FCSTD DOCUMENT  (FreeCAD 1.2R20251216 (Git shallow))
Label: MainAssembly
License: All rights reserved
objects: App::Link×10, App::FeaturePython×8, App::Point×3, Assembly::AssemblyLink×2, Assembly::JointGroup×1, Assembly::AssemblyObject×1
EXTERNAL_REF file=BaseAssembly.FCStd obj=Assembly
EXTERNAL_REF file=BaseAssembly.FCStd obj=Base
EXTERNAL_REF file=BaseAssembly.FCStd obj=Bracket
EXTERNAL_REF file=BaseAssembly.FCStd obj=Bracket001
EXTERNAL_REF file=assembly/BasePart.FCStd obj=Body002

FEATURE [App::Point] Origin001
  Role = Origin
FEATURE [App::Point] Origin003
  Role = Origin
FEATURE [App::Link] Base
  LinkPlacement = pos=(-8,9.53674e-07,0) rot=(0,0,1;0rad)
  LinkedObject = -> <external BaseAssembly.FCStd>#Base
  Placement = pos=(-8,9.53674e-07,0) rot=(0,0,1;0rad)
FEATURE [App::Link] Bracket
  LinkPlacement = pos=(-33,9.53674e-07,5) rot=(0,0,1;0rad)
  LinkedObject = -> <external BaseAssembly.FCStd>#Bracket
  Placement = pos=(-33,9.53674e-07,5) rot=(0,0,1;0rad)
FEATURE [App::Link] Bracket001
  LinkPlacement = pos=(17,9.53674e-07,5) rot=(0,0,1;3.14159rad)
  LinkedObject = -> <external BaseAssembly.FCStd>#Bracket001
  Placement = pos=(17,9.53674e-07,5) rot=(0,0,1;3.14159rad)
FEATURE [Assembly::AssemblyLink] Assembly001  label="Assembly"
  Group = -> [Base,Bracket,Bracket001]
  LinkedObject = -> <external BaseAssembly.FCStd>#Assembly
  Origin = -> Origin002
  Placement = pos=(0,17.655,0) rot=(0,-1,0;0.007806rad)
  Rigid = true
FEATURE [App::FeaturePython] GroundedJoint  # Assembly grounded joint (typed FeaturePython)
  ObjectToGround = -> Assembly001
FEATURE [App::Point] Origin005  label="Origin006"
  Role = Origin
FEATURE [App::Link] Base001
  LinkPlacement = pos=(-8,9.53674e-07,0) rot=(0,0,1;0rad)
  LinkedObject = -> <external BaseAssembly.FCStd>#Base
  Placement = pos=(-8,9.53674e-07,0) rot=(0,0,1;0rad)
FEATURE [App::Link] Bracket002
  LinkPlacement = pos=(-33,9.53674e-07,5) rot=(0,0,1;0rad)
  LinkedObject = -> <external BaseAssembly.FCStd>#Bracket
  Placement = pos=(-33,9.53674e-07,5) rot=(0,0,1;0rad)
FEATURE [App::Link] Bracket003
  LinkPlacement = pos=(17,9.53674e-07,5) rot=(0,0,1;3.14159rad)
  LinkedObject = -> <external BaseAssembly.FCStd>#Bracket001
  Placement = pos=(17,9.53674e-07,5) rot=(0,0,1;3.14159rad)
FEATURE [Assembly::AssemblyLink] Assembly002  label="Assembly 1"
  Group = -> [Base001,Bracket002,Bracket003]
  LinkedObject = -> <external BaseAssembly.FCStd>#Assembly
  Origin = -> Origin004
  Placement = pos=(-0.0157594,146.637,-0.000123025) rot=(0.003785,-0.244485,-0.969646;0.031927rad)
  Rigid = true
FEATURE [App::FeaturePython] Joint  label="Slider"  # Assembly joint (typed FeaturePython)
  Angle = 0
  AngleMax = 0
  AngleMin = 0
  Detach1 = false
  Detach2 = false
  Distance = 0
  Distance2 = 0
  EnableAngleMax = false
  EnableAngleMin = false
  EnableLengthMax = true
  EnableLengthMin = true
  JointType = 3 (Slider)
  LengthMax = 130
  LengthMin = 60
  Placement1 = pos=(-24.8905,0,5) rot=(0.57735,0.57735,0.57735;4.18879rad)
  Placement2 = pos=(-24.8905,0,5) rot=(0.57735,0.57735,0.57735;4.18879rad)
  Reference1 = -> Assembly [Assembly001.Base.Edge12,Assembly001.Base.Edge12]
  Reference2 = -> Assembly [Assembly002.Base001.Edge12,Assembly002.Base001.Edge12]
  Suppressed = false
FEATURE [App::Link] Link
  LinkPlacement = pos=(-31.3123,17.7165,39.7568) rot=(0.312496,0.888118,-0.337035;4.57501rad)
  LinkedObject = -> <external assembly/BasePart.FCStd>#Body002
  Placement = pos=(-31.3123,17.7165,39.7568) rot=(0.312496,0.888118,-0.337035;4.57501rad)
FEATURE [App::FeaturePython] Joint001  label="Revolute"  # Assembly joint (typed FeaturePython)
  Angle = 0
  AngleMax = 0
  AngleMin = 0
  Detach1 = false
  Detach2 = false
  Distance = 0
  Distance2 = 0
  EnableAngleMax = false
  EnableAngleMin = false
  EnableLengthMax = false
  EnableLengthMin = false
  JointType = 1 (Revolute)
  LengthMax = 0
  LengthMin = 0
  Placement1 = pos=(0,-5.3e-15,2) rot=(0,0,1;0rad)
  Placement2 = pos=(0,0,35) rot=(0.57735,0.57735,0.57735;2.0944rad)
  Reference1 = -> Assembly [Link.Edge15,Link.Edge15]
  Reference2 = -> Assembly [Assembly001.Bracket.Edge45,Assembly001.Bracket.Edge45]
  Suppressed = false
FEATURE [App::Link] Link001
  LinkPlacement = pos=(-31.9056,82.7182,115.773) rot=(-0.680956,-0.263231,0.68338;2.66999rad)
  LinkedObject = -> <external assembly/BasePart.FCStd>#Body002
  Placement = pos=(-31.9056,82.7182,115.773) rot=(-0.680956,-0.263231,0.68338;2.66999rad)
FEATURE [App::FeaturePython] Joint002  label="Revolute001"  # Assembly joint (typed FeaturePython)
  Angle = 0
  AngleMax = 0
  AngleMin = 0
  Detach1 = false
  Detach2 = false
  Distance = 0
  Distance2 = 0
  EnableAngleMax = false
  EnableAngleMin = false
  EnableLengthMax = false
  EnableLengthMin = false
  JointType = 1 (Revolute)
  LengthMax = 0
  LengthMin = 0
  Placement1 = pos=(100,2.84e-14,3.6e-15) rot=(0,0,1;0rad)
  Placement2 = pos=(0,0,35) rot=(0.57735,0.57735,0.57735;2.0944rad)
  Reference1 = -> Assembly [Link001.Edge17,Link001.Edge17]
  Reference2 = -> Assembly [Assembly002.Bracket002.Edge45,Assembly002.Bracket002.Edge45]
  Suppressed = false
FEATURE [App::FeaturePython] Joint003  label="Revolute002"  # Assembly joint (typed FeaturePython)
  Angle = 0
  AngleMax = 0
  AngleMin = 0
  Detach1 = false
  Detach2 = false
  Distance = 0
  Distance2 = 0
  EnableAngleMax = false
  EnableAngleMin = false
  EnableLengthMax = false
  EnableLengthMin = false
  JointType = 1 (Revolute)
  LengthMax = 0
  LengthMin = 0
  Placement1 = pos=(-1.42e-14,0,2) rot=(0,0,1;0rad)
  Placement2 = pos=(100,3.6e-15,-3.6e-15) rot=(0,0,1;0rad)
  Reference1 = -> Assembly [Link001.Edge15,Link001.Edge15]
  Reference2 = -> Assembly [Link.Edge17,Link.Edge17]
  Suppressed = false
FEATURE [App::Link] Link002
  LinkPlacement = pos=(16.0768,81.8829,116.802) rot=(-0.307622,0.88959,-0.337636;1.69094rad)
  LinkedObject = -> <external assembly/BasePart.FCStd>#Body002
  Placement = pos=(16.0768,81.8829,116.802) rot=(-0.307622,0.88959,-0.337636;1.69094rad)
FEATURE [App::FeaturePython] Joint004  label="Revolute003"  # Assembly joint (typed FeaturePython)
  Angle = 0
  AngleMax = 0
  AngleMin = 0
  Detach1 = false
  Detach2 = false
  Distance = 0
  Distance2 = 0
  EnableAngleMax = false
  EnableAngleMin = false
  EnableLengthMax = false
  EnableLengthMin = false
  JointType = 1 (Revolute)
  LengthMax = 0
  LengthMin = 0
  Placement1 = pos=(100,1.24e-14,2) rot=(0,0,1;0rad)
  Placement2 = pos=(0,0,35) rot=(0.57735,0.57735,0.57735;2.0944rad)
  Reference1 = -> Assembly [Link002.Edge18,Link002.Edge18]
  Reference2 = -> Assembly [Assembly001.Bracket001.Edge45,Assembly001.Bracket001.Edge45]
  Suppressed = false
FEATURE [App::Link] Link003
  LinkPlacement = pos=(18.6623,146.049,40.1469) rot=(-0.308356,0.891015,0.333179;4.57834rad)
  LinkedObject = -> <external assembly/BasePart.FCStd>#Body002
  Placement = pos=(18.6623,146.049,40.1469) rot=(-0.308356,0.891015,0.333179;4.57834rad)
FEATURE [App::FeaturePython] Joint005  label="Revolute004"  # Assembly joint (typed FeaturePython)
  Angle = 0
  AngleMax = 0
  AngleMin = 0
  Detach1 = false
  Detach2 = false
  Distance = 0
  Distance2 = 0
  EnableAngleMax = false
  EnableAngleMin = false
  EnableLengthMax = false
  EnableLengthMin = false
  JointType = 1 (Revolute)
  LengthMax = 0
  LengthMin = 0
  Placement1 = pos=(0,0,2) rot=(0,0,1;0rad)
  Placement2 = pos=(0,0,35) rot=(0.57735,0.57735,0.57735;2.0944rad)
  Reference1 = -> Assembly [Link003.Edge15,Link003.Edge15]
  Reference2 = -> Assembly [Assembly002.Bracket003.Edge45,Assembly002.Bracket003.Edge45]
  Suppressed = false
FEATURE [App::FeaturePython] Joint006  label="Revolute005"  # Assembly joint (typed FeaturePython)
  Angle = 0
  AngleMax = 0
  AngleMin = 0
  Detach1 = false
  Detach2 = false
  Distance = 0
  Distance2 = 0
  EnableAngleMax = false
  EnableAngleMin = false
  EnableLengthMax = false
  EnableLengthMin = false
  JointType = 1 (Revolute)
  LengthMax = 0
  LengthMin = 0
  Placement1 = pos=(100,0,1.8e-15) rot=(0,0,1;0rad)
  Reference1 = -> Assembly [Link003.Edge17,Link003.Edge17]
  Reference2 = -> Assembly [Link002.Edge3,Link002.Edge3]
  Suppressed = false
FEATURE [Assembly::JointGroup] Joints
  Group = -> [GroundedJoint,Joint,Joint001,Joint002,Joint003,Joint004,Joint005,Joint006]
FEATURE [Assembly::AssemblyObject] Assembly
  Group = -> [Joints,Assembly001,GroundedJoint,Assembly002,Joint,Link,Joint001,Link001,Joint002,Joint003,Link002,Joint004,Link003,Joint005,Joint006]
  Origin = -> Origin
  Type = Assembly

RESOLVED EXTERNAL PARTS (link-assembly join: the EXTERNAL_REF files above that resolve inside this repo's crawl, each included once):
---- part BaseAssembly.FCStd = doc fcstd_8ca3d356e84e ----
FCSTD DOCUMENT  (FreeCAD 1.2R20251216 (Git shallow))
Label: BaseAssembly
License: All rights reserved
objects: App::Link×3, App::FeaturePython×3, App::Point×1, Assembly::JointGroup×1, Assembly::AssemblyObject×1
EXTERNAL_REF file=assembly/BasePart.FCStd obj=Body
EXTERNAL_REF file=assembly/BasePart.FCStd obj=Body001

FEATURE [App::Point] Origin001
  Role = Origin
FEATURE [App::Link] Base
  LinkPlacement = pos=(-8,9.53674e-07,0) rot=(0,0,1;0rad)
  LinkedObject = -> <external assembly/BasePart.FCStd>#Body
  Placement = pos=(-8,9.53674e-07,0) rot=(0,0,1;0rad)
FEATURE [App::FeaturePython] GroundedJoint  # Assembly grounded joint (typed FeaturePython)
  ObjectToGround = -> Base
FEATURE [App::Link] Bracket001
  LinkPlacement = pos=(17,9.53674e-07,5) rot=(0,0,1;3.14159rad)
  LinkedObject = -> <external assembly/BasePart.FCStd>#Body001
  Placement = pos=(17,9.53674e-07,5) rot=(0,0,1;3.14159rad)
FEATURE [App::FeaturePython] Joint001  label="Fixed003"  # Assembly joint (typed FeaturePython)
  Angle = 0
  AngleMax = 0
  AngleMin = 0
  Detach1 = false
  Detach2 = false
  Distance = 0
  Distance2 = 0
  EnableAngleMax = false
  EnableAngleMin = false
  EnableLengthMax = false
  EnableLengthMin = false
  JointType = 0 (Fixed)
  LengthMax = 0
  LengthMin = 0
  Placement1 = pos=(-15,15,0) rot=(0,0,1;0rad)
  Placement2 = pos=(40,-15,5) rot=(0,1,0;3.14159rad)
  Reference1 = -> Assembly [Bracket001.Edge53,Bracket001.Edge53]
  Reference2 = -> Assembly [Base.Edge40,Base.Edge40]
  Suppressed = false
FEATURE [App::FeaturePython] Joint  label="Fixed002"  # Assembly joint (typed FeaturePython)
  Angle = 0
  AngleMax = 0
  AngleMin = 0
  Detach1 = false
  Detach2 = false
  Distance = 0
  Distance2 = 0
  EnableAngleMax = false
  EnableAngleMin = false
  EnableLengthMax = false
  EnableLengthMin = false
  JointType = 0 (Fixed)
  LengthMax = 0
  LengthMin = 0
  Placement1 = pos=(-15,-15,0) rot=(0,0,1;0rad)
  Placement2 = pos=(-40,-15,5) rot=(0,0,1;0rad)
  Reference1 = -> Assembly [Bracket.Edge52,Bracket.Edge52]
  Reference2 = -> Assembly [Base.Edge14,Base.Edge14]
  Suppressed = false
FEATURE [Assembly::JointGroup] Joints
  Group = -> [GroundedJoint,Joint,Joint001]
FEATURE [App::Link] Bracket
  LinkPlacement = pos=(-33,9.53674e-07,5) rot=(0,0,1;0rad)
  LinkedObject = -> <external assembly/BasePart.FCStd>#Body001
  Placement = pos=(-33,9.53674e-07,5) rot=(0,0,1;0rad)
FEATURE [Assembly::AssemblyObject] Assembly
  Group = -> [Joints,Base,GroundedJoint,Bracket,Joint,Bracket001,Joint001]
  Origin = -> Origin
  Type = Assembly
---- part assembly/BasePart.FCStd = doc fcstd_4848bd1dab05 ----
FCSTD DOCUMENT  (FreeCAD 1.2R20251216 (Git shallow))
Label: BasePart
License: All rights reserved
LicenseURL: https://en.wikipedia.org/wiki/All_rights_reserved
objects: Sketcher::SketchObject×6, PartDesign::Pad×5, PartDesign::Body×3, App::Point×3, PartDesign::Pocket×1, PartDesign::Mirrored×1, PartDesign::Chamfer×1
note: 38 computed .brp shape members not serialized (recipe doc carries the construction recipe); baked Part::Feature solids carry a one-line shape summary decoded from their .brp

FEATURE [Sketcher::SketchObject] Sketch
  ArcFitTolerance = 1e-06
  AttachmentSupport = -> [XY_Plane]
  ExternalTypes = [0]
  FullyConstrained = true
  MakeInternals = false
  MapMode = 5
  sketch-geometry (10):
    g0: LineSegment StartX=-50 StartY=15 StartZ=0 EndX=-50 EndY=-15 EndZ=0
    g1: LineSegment StartX=-40 StartY=-25 StartZ=0 EndX=0 EndY=-25 EndZ=0
    g2: LineSegment StartX=0 StartY=-25 StartZ=0 EndX=0 EndY=25 EndZ=0
    g3: LineSegment StartX=0 StartY=25 StartZ=0 EndX=-40 EndY=25 EndZ=0
    g4: ArcOfCircle CenterX=-40 CenterY=15 CenterZ=0 NormalX=0 NormalY=0 NormalZ=1 AngleXU=0 Radius=10 StartAngle=1.5708 EndAngle=3.14159
    g5: GeomPoint [constr] X=-50 Y=25 Z=0
    g6: ArcOfCircle CenterX=-40 CenterY=-15 CenterZ=0 NormalX=0 NormalY=0 NormalZ=1 AngleXU=0 Radius=10 StartAngle=3.14159 EndAngle=4.71239
    g7: GeomPoint [constr] X=-50 Y=-25 Z=0
    g8: Circle CenterX=-40 CenterY=15 CenterZ=0 NormalX=0 NormalY=0 NormalZ=1 AngleXU=0 Radius=5
    g9: Circle CenterX=-40 CenterY=-15 CenterZ=0 NormalX=0 NormalY=0 NormalZ=1 AngleXU=0 Radius=5
  constraints (23):
    c: Coincident(g1,g2)
    c: Coincident(g2,g3)
    c: Vertical(g0)
    c: Vertical(g2)
    c: Horizontal(g1)
    c: Horizontal(g3)
    c: Distance(g5,g2) = 50
    c: Distance(g7,g5) = 50
    c: Symmetric(g2,g1,g-1)
    c: PointOnObject(g5,g0)
    c: PointOnObject(g5,g3)
    c: Tangent(g0,g4) = -1.5708
    c: Tangent(g3,g4) = -1.5708
    c: PointOnObject(g7,g0)
    c: PointOnObject(g7,g1)
    c: Tangent(g0,g6) = -1.5708
    c: Tangent(g1,g6) = -1.5708
    c: Radius(g4) = 10
    c: Equal(g6,g4)
    c: Coincident(g8,g4)
    c: Coincident(g9,g6)
    c: Equal(g8,g9)
    c: Diameter(g8) = 10
FEATURE [PartDesign::Pad] Pad
  Direction = (0,0,1)
  Length = 5
  Length2 = 10
  Profile = -> Sketch
  ReferenceAxis = -> Sketch [N_Axis]
  Refine = true
  SideType = 0
  Suppressed = false
  Type = 0
  Type2 = 0
FEATURE [Sketcher::SketchObject] Sketch001
  ArcFitTolerance = 1e-06
  AttachmentSupport = -> [Pad]
  ExternalGeometry = -> [Pad]
  ExternalTypes = [0]
  FullyConstrained = true
  MakeInternals = false
  MapMode = 5
  Placement = pos=(0,-25,0) rot=(1,0,0;1.5708rad)
  sketch-geometry (4):
    g0: LineSegment StartX=0 StartY=3 StartZ=0 EndX=-24 EndY=3 EndZ=0
    g1: LineSegment StartX=-24 StartY=3 StartZ=0 EndX=-24.8905 EndY=5 EndZ=0
    g2: LineSegment StartX=-24.8905 StartY=5 StartZ=0 EndX=0 EndY=5 EndZ=0
    g3: LineSegment StartX=0 StartY=5 StartZ=0 EndX=0 EndY=3 EndZ=0
  constraints (11):
    c: PointOnObject(g0,g-2)
    c: Horizontal(g0)
    c: Coincident(g0,g1)
    c: PointOnObject(g1,g-3)
    c: Coincident(g1,g2)
    c: Coincident(g2,g-3)
    c: Coincident(g2,g3)
    c: Coincident(g3,g0)
    c: Distance(g3,g3) = 2
    c: DistanceX(g0,g0) = 24
    c: Angle(g0,g1) = 1.98968
FEATURE [PartDesign::Pocket] Pocket
  BaseFeature = -> Pad
  Direction = (0,1,-2e-16)
  Length = 5
  Length2 = 5
  Profile = -> Sketch001
  ReferenceAxis = -> Sketch001 [N_Axis]
  Refine = true
  SideType = 0
  Suppressed = false
  Type = 1
  Type2 = 0
FEATURE [PartDesign::Mirrored] Mirrored
  BaseFeature = -> Pocket
  MirrorPlane = -> YZ_Plane
  Refine = true
  Suppressed = false
  TransformMode = 1
FEATURE [PartDesign::Body] Body  label="Base"
  AllowCompound = false
  Group = -> [Sketch,Pad,Sketch001,Pocket,Mirrored]
  Origin = -> Origin
  Tip = -> Mirrored
FEATURE [Sketcher::SketchObject] Sketch002
  ArcFitTolerance = 1e-06
  AttachmentSupport = -> [XY_Plane001]
  ExternalTypes = [0]
  FullyConstrained = true
  MakeInternals = false
  MapMode = 5
  sketch-geometry (8):
    g0: LineSegment StartX=0 StartY=25 StartZ=0 EndX=-15 EndY=25 EndZ=0
    g1: ArcOfCircle CenterX=-15 CenterY=15 CenterZ=0 NormalX=0 NormalY=0 NormalZ=1 AngleXU=0 Radius=10 StartAngle=1.5708 EndAngle=3.14159
    g2: LineSegment StartX=-25 StartY=15 StartZ=0 EndX=-25 EndY=-15 EndZ=0
    g3: ArcOfCircle CenterX=-15 CenterY=-15 CenterZ=0 NormalX=0 NormalY=0 NormalZ=1 AngleXU=0 Radius=10 StartAngle=3.14159 EndAngle=4.71239
    g4: LineSegment StartX=-15 StartY=-25 StartZ=0 EndX=0 EndY=-25 EndZ=0
    g5: LineSegment StartX=0 StartY=-25 StartZ=0 EndX=0 EndY=25 EndZ=0
    g6: Circle CenterX=-15 CenterY=15 CenterZ=0 NormalX=0 NormalY=0 NormalZ=1 AngleXU=0 Radius=5
    g7: Circle CenterX=-15 CenterY=-15 CenterZ=0 NormalX=0 NormalY=0 NormalZ=1 AngleXU=0 Radius=5
  constraints (19):
    c: PointOnObject(g0,g-2)
    c: Tangent(g0,g1) = -1.5708
    c: Vertical(g2)
    c: Tangent(g2,g3) = -1.5708
    c: Tangent(g3,g4) = -1.5708
    c: Coincident(g4,g5)
    c: Coincident(g5,g0)
    c: Horizontal(g0)
    c: Horizontal(g4)
    c: Tangent(g1,g2) = -1.5708
    c: Coincident(g6,g1)
    c: Coincident(g7,g3)
    c: DistanceX(g1,g0) = 25
    c: DistanceY(g4,g0) = 50
    c: Diameter(g6) = 10
    c: Radius(g1) = 10
    c: Equal(g6,g7)
    c: Equal(g1,g3)
    c: Symmetric(g4,g0,g-1)
FEATURE [PartDesign::Pad] Pad001
  Direction = (0,0,1)
  Length = 5
  Length2 = 10
  Profile = -> Sketch002
  ReferenceAxis = -> Sketch002 [N_Axis]
  Refine = true
  SideType = 0
  Suppressed = false
  Type = 0
  Type2 = 0
FEATURE [Sketcher::SketchObject] Sketch003
  ArcFitTolerance = 1e-06
  AttachmentSupport = -> [Pad001]
  ExternalGeometry = -> [Pad001]
  ExternalTypes = [0]
  FullyConstrained = true
  MakeInternals = false
  MapMode = 5
  Placement = pos=(0,0,0) rot=(0.57735,0.57735,0.57735;2.0944rad)
  sketch-geometry (7):
    g0: LineSegment StartX=-25 StartY=5 StartZ=0 EndX=25 EndY=5 EndZ=0
    g1: ArcOfCircle CenterX=-25 CenterY=20 CenterZ=0 NormalX=0 NormalY=0 NormalZ=1 AngleXU=0 Radius=15 StartAngle=4.71239 EndAngle=6.28319
    g2: ArcOfCircle CenterX=25 CenterY=20 CenterZ=0 NormalX=0 NormalY=0 NormalZ=1 AngleXU=0 Radius=15 StartAngle=3.14159 EndAngle=4.71239
    g3: LineSegment StartX=-10 StartY=20 StartZ=0 EndX=-10 EndY=35 EndZ=0
    g4: LineSegment StartX=10 StartY=20 StartZ=0 EndX=10 EndY=35 EndZ=0
    g5: ArcOfCircle CenterX=0 CenterY=35 CenterZ=0 NormalX=0 NormalY=0 NormalZ=1 AngleXU=0 Radius=10 StartAngle=0 EndAngle=3.14159
    g6: Circle CenterX=0 CenterY=35 CenterZ=0 NormalX=0 NormalY=0 NormalZ=1 AngleXU=0 Radius=2.5
  constraints (15):
    c: Coincident(g0,g-3)
    c: Coincident(g0,g-4)
    c: Vertical(g3)
    c: Vertical(g4)
    c: Tangent(g1,g0) = -1.5708
    c: Tangent(g2,g0) = -1.5708
    c: Tangent(g3,g1) = -1.5708
    c: Tangent(g4,g2) = 1.5708
    c: Tangent(g5,g3) = 1.5708
    c: Tangent(g5,g4) = -1.5708
    c: PointOnObject(g5,g-2)
    c: DistanceY(g0,g5) = 30
    c: Radius(g5) = 10
    c: Diameter(g6) = 5
    c: Coincident(g6,g5)
FEATURE [PartDesign::Pad] Pad002
  BaseFeature = -> Pad001
  Direction = (1,0,0)
  Length = 5
  Length2 = 10
  Profile = -> Sketch003
  ReferenceAxis = -> Sketch003 [N_Axis]
  Refine = true
  Reversed = true
  SideType = 0
  Suppressed = false
  Type = 0
  Type2 = 0
FEATURE [Sketcher::SketchObject] Sketch004
  ArcFitTolerance = 1e-06
  AttachmentSupport = -> [Pad002]
  ExternalGeometry = -> [Pad002]
  ExternalTypes = [0]
  FullyConstrained = true
  MakeInternals = false
  MapMode = 5
  Placement = pos=(-5,0,0) rot=(0.57735,-0.57735,-0.57735;2.0944rad)
  sketch-geometry (4):
    g0: LineSegment StartX=-2.5 StartY=25 StartZ=0 EndX=-2.5 EndY=5 EndZ=0
    g1: LineSegment StartX=-2.5 StartY=5 StartZ=0 EndX=2.5 EndY=5 EndZ=0
    g2: LineSegment StartX=2.5 StartY=5 StartZ=0 EndX=2.5 EndY=25 EndZ=0
    g3: LineSegment StartX=2.5 StartY=25 StartZ=0 EndX=-2.5 EndY=25 EndZ=0
  constraints (11):
    c: Coincident(g0,g1)
    c: Coincident(g1,g2)
    c: Coincident(g2,g3)
    c: Coincident(g3,g0)
    c: Vertical(g0)
    c: Vertical(g2)
    c: Horizontal(g1)
    c: PointOnObject(g1,g-3)
    c: Symmetric(g0,g2,g-2)
    c: Distance(g3,g3) = 5
    c: DistanceY(g2,g2) = 20
FEATURE [PartDesign::Pad] Pad003
  BaseFeature = -> Pad002
  Direction = (-1,0,0)
  Length = 20
  Length2 = 10
  Profile = -> Sketch004
  ReferenceAxis = -> Sketch004 [N_Axis]
  Refine = true
  SideType = 0
  Suppressed = false
  Type = 0
  Type2 = 0
FEATURE [PartDesign::Chamfer] Chamfer
  Angle = 45
  Base = -> Pad003 [Edge54]
  BaseFeature = -> Pad003
  ChamferType = 0
  FlipDirection = false
  Refine = true
  Size = 19.99
  Size2 = 1
  SupportTransform = false
  Suppressed = false
  UseAllEdges = false
FEATURE [PartDesign::Body] Body001  label="Bracket"
  AllowCompound = false
  Group = -> [Sketch002,Pad001,Sketch003,Pad002,Sketch004,Pad003,Chamfer]
  Origin = -> Origin001
  Placement = pos=(0,62.122,0) rot=(0,0,1;0rad)
  Tip = -> Chamfer
FEATURE [App::Point] Origin002  label="Origin"
  Role = Origin
FEATURE [App::Point] Origin003  label="Origin"
  Role = Origin
FEATURE [App::Point] Origin005
  Role = Origin
FEATURE [Sketcher::SketchObject] Sketch005
  ArcFitTolerance = 1e-06
  AttachmentSupport = -> [Origin004]
  ExternalTypes = [0]
  FullyConstrained = true
  MakeInternals = false
  MapMode = 5
  sketch-geometry (6):
    g0: ArcOfCircle CenterX=0 CenterY=0 CenterZ=0 NormalX=0 NormalY=0 NormalZ=1 AngleXU=0 Radius=8 StartAngle=1.5708 EndAngle=4.71239
    g1: ArcOfCircle CenterX=100 CenterY=0 CenterZ=0 NormalX=0 NormalY=0 NormalZ=1 AngleXU=0 Radius=8 StartAngle=4.71239 EndAngle=7.85398
    g2: LineSegment StartX=-1.114e-13 StartY=8 StartZ=0 EndX=100 EndY=8 EndZ=0
    g3: LineSegment StartX=-1.081e-13 StartY=-8 StartZ=0 EndX=100 EndY=-8 EndZ=0
    g4: Circle CenterX=0 CenterY=0 CenterZ=0 NormalX=0 NormalY=0 NormalZ=1 AngleXU=0 Radius=2.5
    g5: Circle CenterX=100 CenterY=0 CenterZ=0 NormalX=0 NormalY=0 NormalZ=1 AngleXU=0 Radius=2.5
  constraints (13):
    c: Tangent(g0,g2) = 1.5708
    c: Tangent(g0,g3) = -1.5708
    c: Tangent(g1,g2) = 1.5708
    c: Tangent(g1,g3) = -1.5708
    c: Equal(g0,g1)
    c: Radius(g0) = 8
    c: Coincident(g0,g-1)
    c: PointOnObject(g1,g-1)
    c: Coincident(g4,g0)
    c: Coincident(g5,g1)
    c: Diameter(g4) = 5
    c: Equal(g4,g5)
    c: DistanceX(g0,g1) = 100
FEATURE [PartDesign::Pad] Pad004
  Direction = (0,0,1)
  Length = 2
  Length2 = 10
  Profile = -> Sketch005
  ReferenceAxis = -> Sketch005 [N_Axis]
  Refine = true
  SideType = 0
  Suppressed = false
  Type = 0
  Type2 = 0
FEATURE [PartDesign::Body] Body002  label="Link"
  AllowCompound = true
  Group = -> [Sketch005,Pad004]
  Origin = -> Origin004
  Placement = pos=(0,86.082,0) rot=(0,0,1;0rad)
  Tip = -> Pad004
